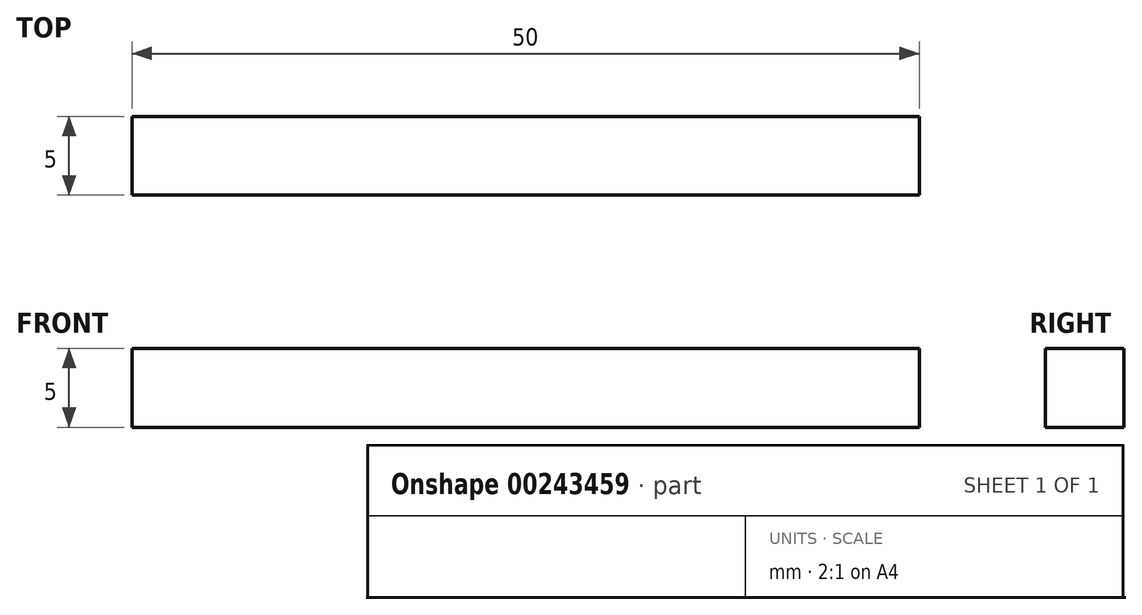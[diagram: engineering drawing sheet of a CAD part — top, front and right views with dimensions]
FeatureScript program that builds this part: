
annotation { "Feature Type Name" : "Feature", "Feature Type Description" : "" }
export const myFeature = defineFeature(function(context is Context, id is Id, definition is map)
    precondition{}
    {
        {
            var Q0;
            Q0=qCreatedBy(makeId("Front.planeOp"),FACE);
            var sketch = newSketch(context, id + "F0", { "sketchPlane" : qUnion([Q0])});
            skLineSegment(sketch, "E0", {"start": v(-66.32, 16.4) * mm, "end": v(-16.32, 16.4) * mm});
            skLineSegment(sketch, "E1", {"start": v(-16.32, 16.4) * mm, "end": v(-16.32, 11.4) * mm});
            skLineSegment(sketch, "E2", {"start": v(-16.32, 11.4) * mm, "end": v(-66.32, 11.4) * mm});
            skLineSegment(sketch, "E3", {"start": v(-66.32, 11.4) * mm, "end": v(-66.32, 16.4) * mm});
            skSolve(sketch);
        }
        {
            var Q0;
            Q0=makeQuery(id+"F0.imprint","IMPRINT",FACE,{"disambiguationData":[TD([[makeQuery(id+"F0.imprint","IMPRINT",EDGE,{"derivedFrom":sQuery(id+"F0.wireOp",EDGE,"E0")}),-1.0]])]});
            extrude(context, id + "F1", {"entities" : qUnion([Q0]), "oppositeDirection" : true, "depth" : 5 * mm, "offsetDistance" : 25 * mm});
        }
    });
